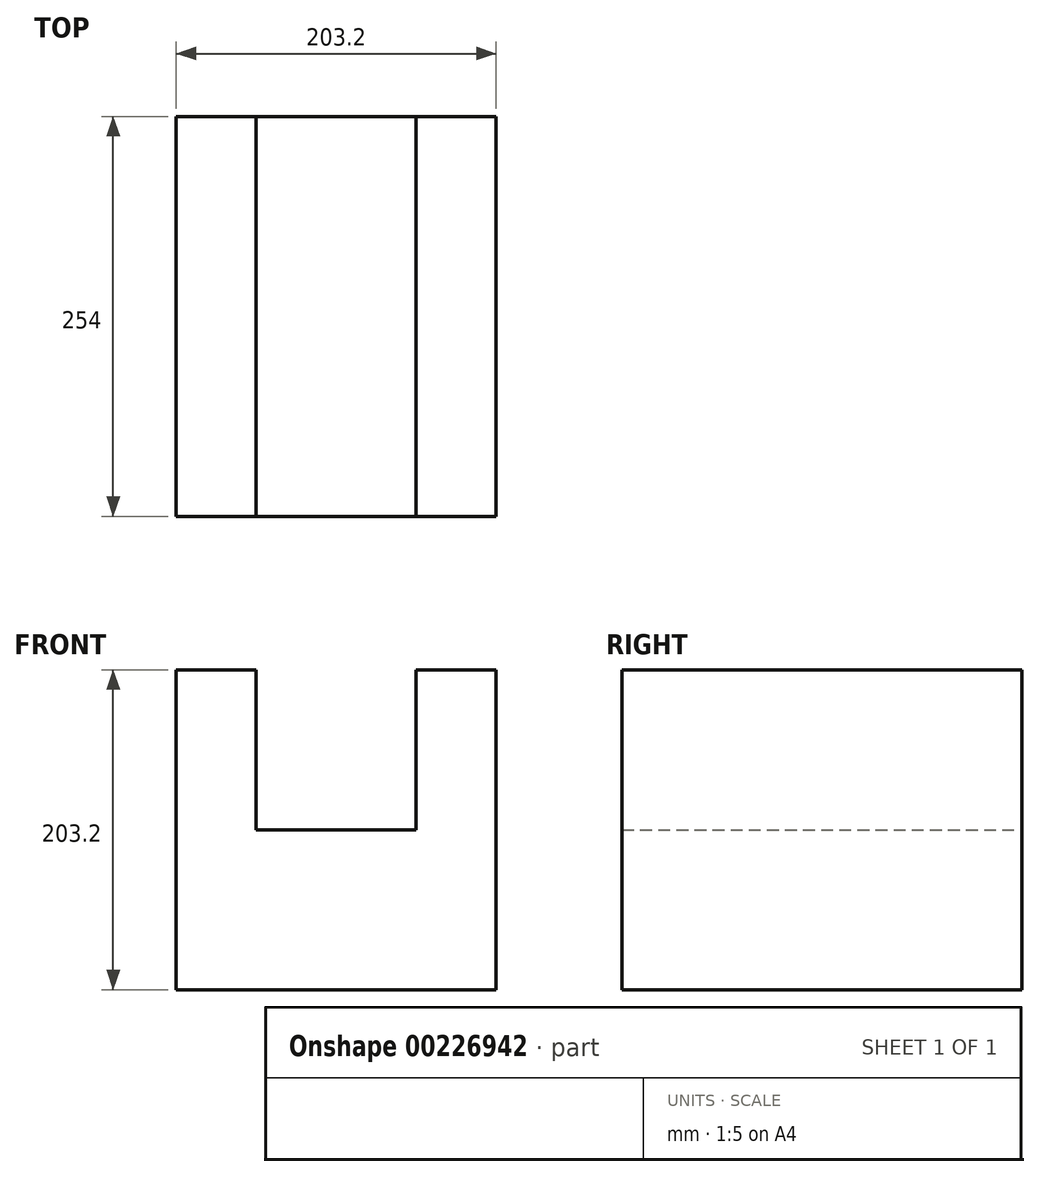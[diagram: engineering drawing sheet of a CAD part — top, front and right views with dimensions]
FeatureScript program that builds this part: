
annotation { "Feature Type Name" : "Feature", "Feature Type Description" : "" }
export const myFeature = defineFeature(function(context is Context, id is Id, definition is map)
    precondition{}
    {
        {
            var Q0;
            Q0=qCreatedBy(makeId("Front.planeOp"),FACE);
            var sketch = newSketch(context, id + "F0", { "sketchPlane" : qUnion([Q0])});
            skLineSegment(sketch, "E0.top", {"start": v(-130.43, -96.42) * mm, "end": v(72.77, -96.42) * mm});
            skLineSegment(sketch, "E0.left", {"start": v(-130.43, 106.78) * mm, "end": v(-130.43, -96.42) * mm});
            skLineSegment(sketch, "E0.right", {"start": v(72.77, 106.78) * mm, "end": v(72.77, -96.42) * mm});
            skLineSegment(sketch, "E1", {"start": v(-79.63, 106.78) * mm, "end": v(-79.63, 5.18) * mm});
            skLineSegment(sketch, "E2", {"start": v(-79.63, 5.18) * mm, "end": v(21.97, 5.18) * mm});
            skLineSegment(sketch, "E3", {"start": v(21.97, 5.18) * mm, "end": v(21.97, 106.78) * mm});
            skLineSegment(sketch, "E4", {"start": v(-130.43, 106.78) * mm, "end": v(-79.63, 106.78) * mm});
            skLineSegment(sketch, "E5", {"start": v(21.97, 106.78) * mm, "end": v(72.77, 106.78) * mm});
            skSolve(sketch);
        }
        {
            var Q0;
            Q0=makeQuery(id+"F0.imprint","IMPRINT",FACE,{"disambiguationData":[TD([[makeQuery(id+"F0.imprint","IMPRINT",EDGE,{"derivedFrom":sQuery(id+"F0.wireOp",EDGE,"E0.top")}),1.0]])]});
            extrude(context, id + "F1", {"entities" : qUnion([Q0]), "depth" : 254 * mm});
        }
    });
